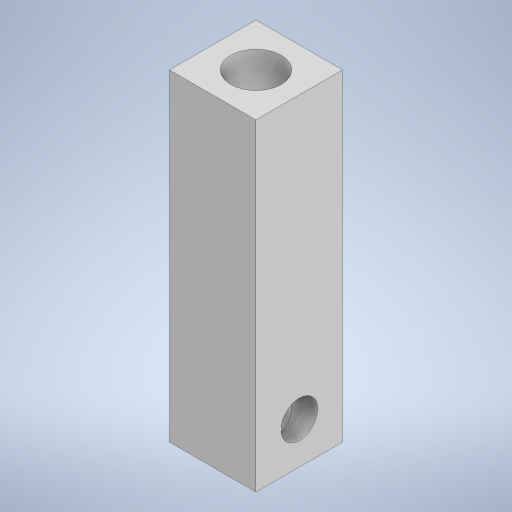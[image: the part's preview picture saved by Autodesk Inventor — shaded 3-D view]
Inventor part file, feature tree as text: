
AUTODESK INVENTOR PART (.ipt)
format: ipt  version: 2024.2 (Build 282272000, 272)  size: 227,840 bytes
history: native  units: mm
features: extrude x3, sketch x3
ambient origin geometry x8: Origin, YZ Plane, XZ Plane, XY Plane, X Axis, Y Axis, Z Axis, Center Point
bodies: Solid1 (feature_tree)
feature tree (6):
  extrude  "Extrusion1"  Depth=9.4mm
  extrude  "Extrusion2"  Depth=35.0mm
  extrude  "Extrusion3"  Depth=4.0mm
  sketch  "Sketch1"  dims[d0=9.4mm d1=9.4mm]
  sketch  "Sketch2"  dims[d2=35.0mm d3=0.0mm d4=5.5mm]
  sketch  "Sketch3"  dims[d5=30.0mm d6=0.0mm d7=4.0mm d8=4.5mm d9=5.0mm d10=0.0mm]
